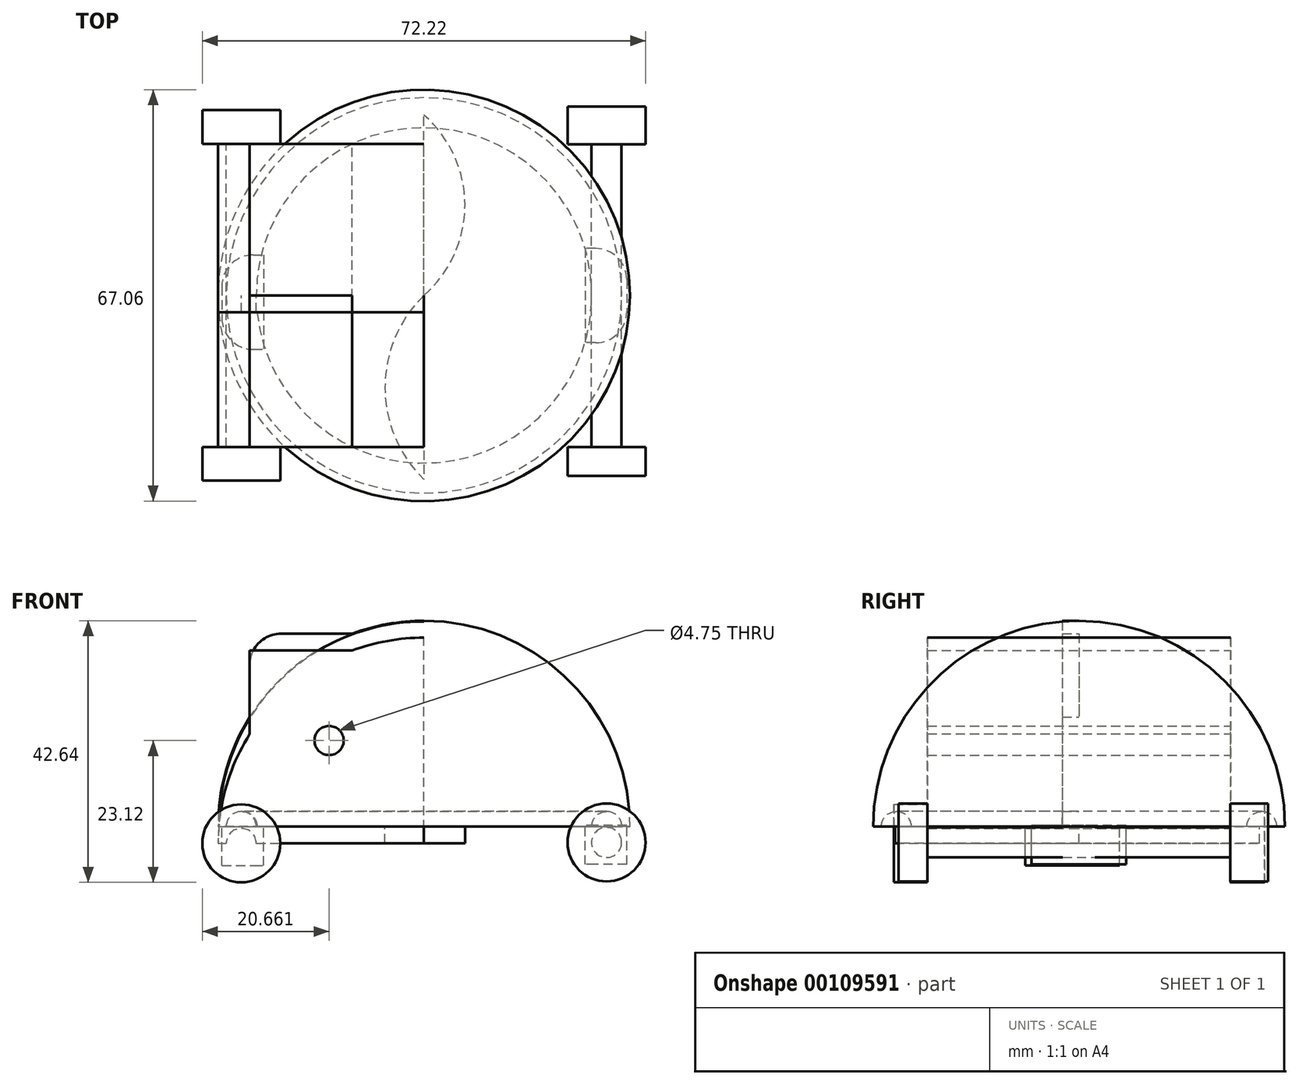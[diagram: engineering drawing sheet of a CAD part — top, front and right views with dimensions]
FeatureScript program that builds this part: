
annotation { "Feature Type Name" : "Feature", "Feature Type Description" : "" }
export const myFeature = defineFeature(function(context is Context, id is Id, definition is map)
    precondition{}
    {
        {
            var Q0;
            Q0=qCreatedBy(makeId("Front.planeOp"),FACE);
            var sketch = newSketch(context, id + "F0", { "sketchPlane" : qUnion([Q0])});
            skLineSegment(sketch, "E0", {"start": v(-43.3, 24.97) * mm, "end": v(23.77, 24.97) * mm});
            skArc(sketch, "E1", {"start": v(23.77, 24.97) * mm, "mid": v(9.37, 52.5) * mm, "end": v(-21.47, 56.4) * mm});
            skLineSegment(sketch, "E2", {"start": v(-9.76, 24.97) * mm, "end": v(-9.76, 58.5) * mm});
            skLineSegment(sketch, "E3", {"start": v(-21.47, 56.4) * mm, "end": v(-38.16, 56.4) * mm});
            skArc(sketch, "E4.trimOffspring", {"start": v(-38.16, 42.81) * mm, "mid": v(-41.99, 34.25) * mm, "end": v(-43.3, 24.97) * mm});
            skLineSegment(sketch, "E5", {"start": v(-38.16, 56.4) * mm, "end": v(-38.16, 42.81) * mm});
            skCircle(sketch, "E6", {"center": v(-25.23, 41.73) * mm, "radius": 2.38 * mm});
            skPoint(sketch, "E6.centerSnap0", {"position": v(-9.76, 41.73) * mm});
            skCircle(sketch, "E7", {"center": v(-39.54, 24.97) * mm, "radius": 2.45 * mm});
            skCircle(sketch, "E8.MirrorC", {"center": v(20.01, 24.97) * mm, "radius": 2.45 * mm});
            skSolve(sketch);
        }
        {
            var Q0;
            {var subQ3=sQuery(id+"F0.wireOp",EDGE,"E2");Q0=makeQuery(id+"F0.imprint","IMPRINT",FACE,{"disambiguationData":[TD([[makeQuery(id+"F0.imprint","IMPRINT",EDGE,{"derivedFrom":subQ3}),-1.0]])]});}
            var Q1;
            Q1=sQuery(id+"F0.wireOp",EDGE,"E2");
            revolve(context, id + "F1", {"entities" : qUnion([Q0]), "axis" : qUnion([Q1]), "revolveType" : RevolveType.FULL});
        }
        {
            var Q0;
            {var subQ0=sQuery(id+"F0.wireOp",EDGE,"E3");Q0=makeQuery(id+"F0.imprint","IMPRINT",FACE,{"disambiguationData":[TD([[makeQuery(id+"F0.imprint","IMPRINT",EDGE,{"derivedFrom":subQ0}),1.0]])]});}
            extrude(context, id + "F2", {"entities" : qUnion([Q0]), "operationType" : NewBodyOperationType.ADD, "depth" : 2.73 * mm});
        }
        {
            var Q0;
            Q0=makeQuery(id+"FCyuBcCmGWLWVZP_1.opExtrude","CAP_EDGE",EDGE,{"disambiguationData":[OSD([sQuery(id+"FPGC2tfeTrthGrM_1.wireOp",EDGE,"Nrsmrp8E-MxX1-JOqs-Gpzh-MylzOGBia1CY")])],"isStart":false});
            var Q1;
            Q1=makeQuery(id+"F2.opExtrude","SWEPT_EDGE",EDGE,{"disambiguationData":[OSD([sQuery(id+"F0.wireOp",EDGE,"E3"),sQuery(id+"F0.wireOp",EDGE,"E5")])]});
            fillet(context, id + "F3", {"entities" : qUnion([Q0, Q1]), "radius" : 5.08 * mm, "tangentPropagation" : true, "allowEdgeOverflow" : false});
        }
        {
            var Q0;
            {var subQ0=sQuery(id+"F0.wireOp",EDGE,"E7");var subQ1=sQuery(id+"F0.wireOp",EDGE,"E0");var subQ2=makeQuery(id+"F0.imprint","INTERSECT",VERTEX,{"disambiguationData":[OD(0.0)],"derivedFrom":[subQ1,subQ0]});Q0=makeQuery(id+"F0.imprint","IMPRINT",FACE,{"disambiguationData":[TD([[makeQuery(id+"F0.imprint","IMPRINT",EDGE,{"disambiguationData":[TD([[subQ2,-1.0]])],"derivedFrom":subQ1}),-1.0]])]});}
            var Q1;
            {var subQ0=sQuery(id+"F0.wireOp",EDGE,"E7");var subQ1=sQuery(id+"F0.wireOp",EDGE,"E0");var subQ2=makeQuery(id+"F0.imprint","INTERSECT",VERTEX,{"disambiguationData":[OD(0.0)],"derivedFrom":[subQ1,subQ0]});Q1=makeQuery(id+"F0.imprint","IMPRINT",FACE,{"disambiguationData":[TD([[makeQuery(id+"F0.imprint","IMPRINT",EDGE,{"disambiguationData":[TD([[subQ2,-1.0]])],"derivedFrom":subQ1}),1.0]])]});}
            var Q2;
            {var subQ0=sQuery(id+"F0.wireOp",EDGE,"E8.MirrorC");var subQ1=sQuery(id+"F0.wireOp",EDGE,"E0");var subQ2=makeQuery(id+"F0.imprint","INTERSECT",VERTEX,{"disambiguationData":[OD(0.0)],"derivedFrom":[subQ1,subQ0]});Q2=makeQuery(id+"F0.imprint","IMPRINT",FACE,{"disambiguationData":[TD([[makeQuery(id+"F0.imprint","IMPRINT",EDGE,{"disambiguationData":[TD([[subQ2,-1.0]])],"derivedFrom":subQ1}),1.0]])]});}
            var Q3;
            {var subQ0=sQuery(id+"F0.wireOp",EDGE,"E8.MirrorC");var subQ1=sQuery(id+"F0.wireOp",EDGE,"E0");var subQ2=makeQuery(id+"F0.imprint","INTERSECT",VERTEX,{"disambiguationData":[OD(0.0)],"derivedFrom":[subQ1,subQ0]});Q3=makeQuery(id+"F0.imprint","IMPRINT",FACE,{"disambiguationData":[TD([[makeQuery(id+"F0.imprint","IMPRINT",EDGE,{"disambiguationData":[TD([[subQ2,-1.0]])],"derivedFrom":subQ1}),-1.0]])]});}
            extrude(context, id + "F4", {"entities" : qUnion([Q0, Q1, Q2, Q3]), "endBound" : BoundingType.SYMMETRIC, "depth" : 49.38 * mm});
        }
        {
            var Q0;
            Q0=makeQuery(id+"F4.opExtrude","CAP_FACE",FACE,{"disambiguationData":[OSD([sQuery(id+"F0.wireOp",EDGE,"E7")])],"isStart":false});
            var sketch = newSketch(context, id + "F5", { "sketchPlane" : qUnion([Q0])});
            skCircle(sketch, "E9", {"center": v(-39.54, 24.97) * mm, "radius": 6.35 * mm});
            skSolve(sketch);
        }
        {
            var Q0;
            Q0 = qSketchRegion(id + "F5", true);
            extrude(context, id + "F6", {"entities" : qUnion([Q0]), "depth" : 5.47 * mm});
        }
        {
            var Q0;
            Q0=makeQuery(id+"F4.opExtrude","CAP_FACE",FACE,{"disambiguationData":[OSD([sQuery(id+"F0.wireOp",EDGE,"E7")])],"isStart":true});
            var sketch = newSketch(context, id + "F7", { "sketchPlane" : qUnion([Q0])});
            skCircle(sketch, "E10", {"center": v(39.54, 24.97) * mm, "radius": 6.35 * mm});
            skSolve(sketch);
        }
        {
            var Q0;
            Q0 = qSketchRegion(id + "F7", true);
            extrude(context, id + "F8", {"entities" : qUnion([Q0]), "depth" : 5.5 * mm});
        }
        {
            var Q0;
            Q0=makeQuery(id+"F4.opExtrude","CAP_FACE",FACE,{"disambiguationData":[OSD([sQuery(id+"F0.wireOp",EDGE,"E8.MirrorC")])],"isStart":true});
            var sketch = newSketch(context, id + "F9", { "sketchPlane" : qUnion([Q0])});
            skCircle(sketch, "E11", {"center": v(-20.01, 24.97) * mm, "radius": 6.35 * mm});
            skSolve(sketch);
        }
        {
            var Q0;
            Q0 = qSketchRegion(id + "F9", true);
            extrude(context, id + "F10", {"entities" : qUnion([Q0]), "depth" : 6.15 * mm});
        }
        {
            var Q0;
            Q0=makeQuery(id+"F4.opExtrude","CAP_FACE",FACE,{"disambiguationData":[OSD([sQuery(id+"F0.wireOp",EDGE,"E8.MirrorC")])],"isStart":false});
            var sketch = newSketch(context, id + "F11", { "sketchPlane" : qUnion([Q0])});
            skCircle(sketch, "E12", {"center": v(20.01, 24.97) * mm, "radius": 6.35 * mm});
            skSolve(sketch);
        }
        {
            var Q0;
            Q0 = qSketchRegion(id + "F11", true);
            extrude(context, id + "F12", {"entities" : qUnion([Q0]), "depth" : 4.66 * mm});
        }
        {
            var Q0;
            Q0=makeQuery(id+"F6.opExtrude","SWEPT_BODY",BODY,{"disambiguationData":[OSD([sQuery(id+"F5.wireOp",EDGE,"E9")])]});
            var Q1;
            Q1=makeQuery(id+"F4.opExtrude","SWEPT_BODY",BODY,{"disambiguationData":[OSD([sQuery(id+"F0.wireOp",EDGE,"E7")])]});
            var Q2;
            Q2=makeQuery(id+"F8.opExtrude","SWEPT_BODY",BODY,{"disambiguationData":[OSD([sQuery(id+"F7.wireOp",EDGE,"E10")])]});
            var Q3;
            Q3=makeQuery(id+"F2.opExtrude","CAP_VERTEX",VERTEX,{"disambiguationData":[OSD([sQuery(id+"F0.wireOp",EDGE,"E4.trimOffspring"),sQuery(id+"F0.wireOp",EDGE,"E5")])],"isStart":false});
            transform(context, id + "F13", {"entities" : qUnion([Q0, Q1, Q2]), "transformType" : TransformType.TRANSLATION_3D, "dx" : 0 * mm, "dy" : 0 * mm, "dz" : -2.75 * mm, "makeCopy" : false});
        }
        {
            var Q0;
            {var subQ0=sQuery(id+"F0.wireOp",EDGE,"E0");Q0=makeQuery(id+"F2.boolean.opBoolean","MERGE",FACE,{"derivedFrom":[makeQuery(id+"F1.opRevolve","SWEPT_FACE",FACE,{"disambiguationData":[OSD([subQ0]),TDD([makeQuery(id+"F0.imprint","IMPRINT",EDGE,{"disambiguationData":[TD([[makeQuery(id+"F0.imprint","INTERSECT",VERTEX,{"derivedFrom":[subQ0,sQuery(id+"F0.wireOp",EDGE,"E1")]}),1.0]])],"derivedFrom":subQ0})])]}),makeQuery(id+"F2.opExtrude","SWEPT_FACE",FACE,{"disambiguationData":[OSD([subQ0]),TDD([makeQuery(id+"F0.imprint","IMPRINT",EDGE,{"disambiguationData":[TD([[makeQuery(id+"F0.imprint","INTERSECT",VERTEX,{"derivedFrom":[subQ0,sQuery(id+"F0.wireOp",EDGE,"E4.trimOffspring")]}),-1.0]])],"derivedFrom":subQ0})])]})]});}
            var sketch = newSketch(context, id + "F14", { "sketchPlane" : qUnion([Q0])});
            skLineSegment(sketch, "E13.bottom", {"start": v(-43.19, 2.73) * mm, "end": v(-36.41, 2.73) * mm});
            skLineSegment(sketch, "E13.top", {"start": v(-43.19, 18.1) * mm, "end": v(-36.41, 18.1) * mm});
            skLineSegment(sketch, "E13.left", {"start": v(-43.19, 2.73) * mm, "end": v(-43.19, 18.1) * mm});
            skLineSegment(sketch, "E13.right", {"start": v(-36.41, 2.73) * mm, "end": v(-36.41, 18.1) * mm});
            skSolve(sketch);
        }
        {
            var Q0;
            Q0 = qSketchRegion(id + "F14", true);
            extrude(context, id + "F15", {"entities" : qUnion([Q0]), "depth" : 6.35 * mm});
        }
        {
            var Q0;
            Q0=makeQuery(id+"F15.opExtrude","SWEPT_BODY",BODY,{"disambiguationData":[OSD([sQuery(id+"F14.wireOp",EDGE,"E13.bottom"),sQuery(id+"F14.wireOp",EDGE,"E13.top"),sQuery(id+"F14.wireOp",EDGE,"E13.left"),sQuery(id+"F14.wireOp",EDGE,"E13.right")])]});
            var Q1;
            Q1=makeQuery(id+"F2.opExtrude","CAP_VERTEX",VERTEX,{"disambiguationData":[OSD([sQuery(id+"F0.wireOp",EDGE,"E0"),sQuery(id+"F0.wireOp",EDGE,"E4.trimOffspring")])],"isStart":true});
            transform(context, id + "F16", {"entities" : qUnion([Q0]), "transformType" : TransformType.TRANSLATION_3D, "dx" : 0.5 * mm, "dy" : 9.32 * mm, "dz" : 0 * mm, "makeCopy" : false});
        }
        {
            var Q0;
            Q0=makeQuery(id+"F15.opExtrude","SWEPT_BODY",BODY,{"disambiguationData":[OSD([sQuery(id+"F14.wireOp",EDGE,"E13.bottom"),sQuery(id+"F14.wireOp",EDGE,"E13.top"),sQuery(id+"F14.wireOp",EDGE,"E13.left"),sQuery(id+"F14.wireOp",EDGE,"E13.right")])]});
            var Q1;
            Q1=qCreatedBy(makeId("Right.planeOp"),FACE);
            mirror(context, id + "F17", {"entities" : qUnion([Q0]), "mirrorPlane" : qUnion([Q1])});
        }
        {
            var Q0;
            Q0=makeQuery(id+"F17.opPattern","COPY",BODY,{"derivedFrom":makeQuery(id+"F15.opExtrude","SWEPT_BODY",BODY,{"disambiguationData":[OSD([sQuery(id+"F14.wireOp",EDGE,"E13.bottom"),sQuery(id+"F14.wireOp",EDGE,"E13.top"),sQuery(id+"F14.wireOp",EDGE,"E13.left"),sQuery(id+"F14.wireOp",EDGE,"E13.right")])]}),"instanceName":"1"});
            var Q1;
            Q1=makeQuery(id+"F17.opPattern","COPY",VERTEX,{"derivedFrom":makeQuery(id+"F15.opExtrude","CAP_VERTEX",VERTEX,{"disambiguationData":[OSD([sQuery(id+"F0.wireOp",EDGE,"E0"),sQuery(id+"F0.wireOp",EDGE,"E8.MirrorC"),sQuery(id+"F14.wireOp",EDGE,"E13.top"),sQuery(id+"F14.wireOp",EDGE,"E13.right")])],"isStart":false}),"instanceName":"1"});
            transform(context, id + "F18", {"entities" : qUnion([Q0]), "transformType" : TransformType.TRANSLATION_3D, "dx" : -19.43 * mm, "dy" : 1.06 * mm, "dz" : 0.18 * mm, "makeCopy" : false});
        }
        {
            var Q0;
            Q0=makeQuery(id+"F4.opExtrude","SWEPT_BODY",BODY,{"disambiguationData":[OSD([sQuery(id+"F0.wireOp",EDGE,"E8.MirrorC")])]});
            var Q1;
            Q1=makeQuery(id+"F12.opExtrude","SWEPT_BODY",BODY,{"disambiguationData":[OSD([sQuery(id+"F11.wireOp",EDGE,"E12")])]});
            var Q2;
            Q2=makeQuery(id+"F10.opExtrude","SWEPT_BODY",BODY,{"disambiguationData":[OSD([sQuery(id+"F9.wireOp",EDGE,"E11")])]});
            var Q3;
            Q3=sQuery(id+"F0.wireOp",VERTEX,"E1.start");
            transform(context, id + "F19", {"entities" : qUnion([Q0, Q1, Q2]), "transformType" : TransformType.TRANSLATION_3D, "dx" : -0.04 * mm, "dy" : -0.04 * mm, "dz" : -2.6 * mm, "makeCopy" : false});
        }
        {
            var Q0;
            Q0=makeQuery(id+"F15.opExtrude","SWEPT_EDGE",EDGE,{"disambiguationData":[OSD([sQuery(id+"F14.wireOp",EDGE,"E13.top"),sQuery(id+"F14.wireOp",EDGE,"E13.left")])]});
            var Q1;
            Q1=makeQuery(id+"F15.opExtrude","SWEPT_EDGE",EDGE,{"disambiguationData":[OSD([sQuery(id+"F0.wireOp",EDGE,"E0"),sQuery(id+"F0.wireOp",EDGE,"E1"),sQuery(id+"F14.wireOp",EDGE,"E13.bottom"),sQuery(id+"F14.wireOp",EDGE,"E13.left")])]});
            var Q2;
            Q2=makeQuery(id+"F17.opPattern","COPY",EDGE,{"derivedFrom":makeQuery(id+"F15.opExtrude","SWEPT_EDGE",EDGE,{"disambiguationData":[OSD([sQuery(id+"F0.wireOp",EDGE,"E0"),sQuery(id+"F0.wireOp",EDGE,"E1"),sQuery(id+"F14.wireOp",EDGE,"E13.bottom"),sQuery(id+"F14.wireOp",EDGE,"E13.left")])]}),"instanceName":"1"});
            var Q3;
            Q3=makeQuery(id+"F17.opPattern","COPY",EDGE,{"derivedFrom":makeQuery(id+"F15.opExtrude","SWEPT_EDGE",EDGE,{"disambiguationData":[OSD([sQuery(id+"F14.wireOp",EDGE,"E13.top"),sQuery(id+"F14.wireOp",EDGE,"E13.left")])]}),"instanceName":"1"});
            fillet(context, id + "F20", {"entities" : qUnion([Q0, Q1, Q2, Q3]), "radius" : 5.08 * mm, "tangentPropagation" : true, "allowEdgeOverflow" : false});
        }
        {
            var Q0;
            {var subQ0=sQuery(id+"F0.wireOp",EDGE,"E0");var subQ1=makeQuery(id+"F0.imprint","INTERSECT",VERTEX,{"derivedFrom":[subQ0,sQuery(id+"F0.wireOp",EDGE,"E2")]});Q0=makeQuery(id+"F2.boolean.opBoolean","MERGE",FACE,{"derivedFrom":[makeQuery(id+"F1.opRevolve","SWEPT_FACE",FACE,{"disambiguationData":[OSD([subQ0]),TDD([makeQuery(id+"F0.imprint","IMPRINT",EDGE,{"disambiguationData":[TD([[subQ1,-1.0]])],"derivedFrom":subQ0})])]}),makeQuery(id+"F2.opExtrude","SWEPT_FACE",FACE,{"disambiguationData":[OSD([subQ0]),TDD([makeQuery(id+"F0.imprint","IMPRINT",EDGE,{"disambiguationData":[TD([[subQ1,1.0]])],"derivedFrom":subQ0})])]})]});}
            var sketch = newSketch(context, id + "F21", { "sketchPlane" : qUnion([Q0])});
            skLineSegment(sketch, "E14", {"start": v(-9.76, 0) * mm, "end": v(-9.76, 30) * mm});
            skLineSegment(sketch, "E15", {"start": v(-9.76, 0) * mm, "end": v(-9.76, -29.4) * mm});
            skArc(sketch, "E16", {"start": v(-9.76, -29.4) * mm, "mid": v(-3.1, -14.7) * mm, "end": v(-9.76, 0) * mm});
            skArc(sketch, "E17", {"start": v(-9.76, 30) * mm, "mid": v(-16.12, 15) * mm, "end": v(-9.76, 0) * mm});
            skSolve(sketch);
        }
        {
            var Q0;
            Q0 = qSketchRegion(id + "F21", true);
            extrude(context, id + "F22", {"entities" : qUnion([Q0]), "depth" : 2.73 * mm});
        }
    });
